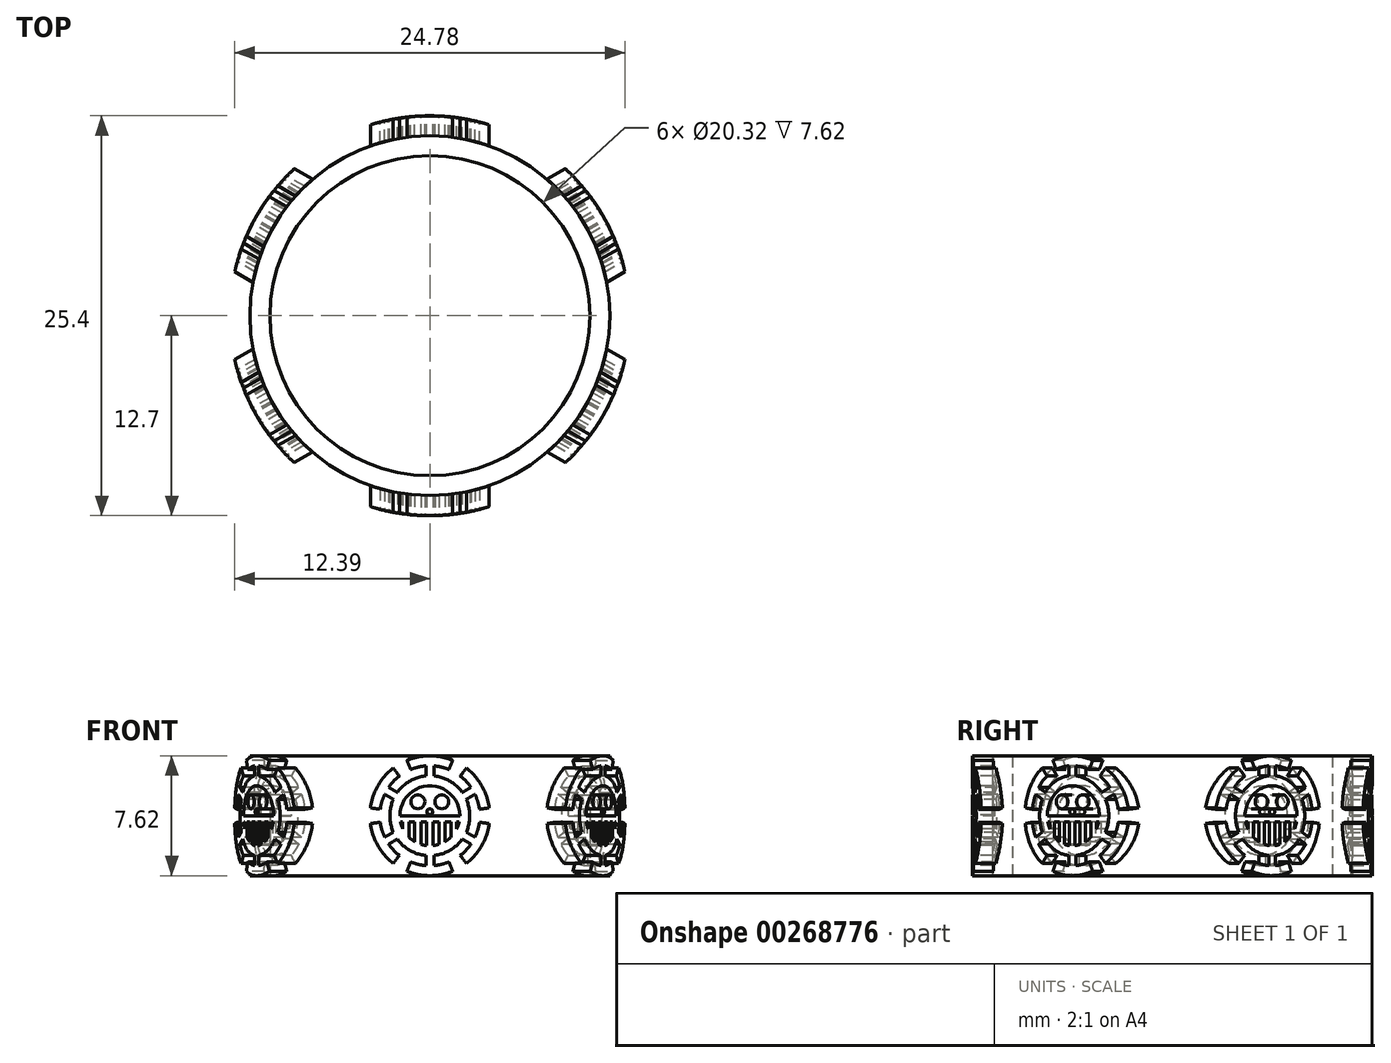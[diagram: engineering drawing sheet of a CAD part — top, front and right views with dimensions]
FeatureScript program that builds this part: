
annotation { "Feature Type Name" : "Feature", "Feature Type Description" : "" }
export const myFeature = defineFeature(function(context is Context, id is Id, definition is map)
    precondition{}
    {
        {
            var Q0;
            Q0=qCreatedBy(makeId("Front.planeOp"),FACE);
            var sketch = newSketch(context, id + "F0", { "sketchPlane" : qUnion([Q0])});
            skCircle(sketch, "E0", {"center": v(0, 3.81) * mm, "radius": 3.81 * mm});
            skSolve(sketch);
        }
        {
            var Q0;
            Q0 = qSketchRegion(id + "F0", true);
            extrude(context, id + "F1", {"entities" : qUnion([Q0]), "depth" : 13.97 * mm});
        }
        {
            var Q0;
            Q0=makeQuery(id+"F1.opExtrude","CAP_FACE",FACE,{"disambiguationData":[OSD([sQuery(id+"F0.wireOp",EDGE,"E0")])],"isStart":false});
            var sketch = newSketch(context, id + "F2", { "sketchPlane" : qUnion([Q0])});
            skArc(sketch, "E1", {"start": v(-1.93, 6.33) * mm, "mid": v(-2.3, 6) * mm, "end": v(-2.61, 5.61) * mm});
            skLineSegment(sketch, "E2", {"start": v(-1.22, 6.74) * mm, "end": v(-1.46, 7.33) * mm});
            skLineSegment(sketch, "E3", {"start": v(1.22, 6.74) * mm, "end": v(1.46, 7.33) * mm});
            skLineSegment(sketch, "E4.1.0", {"start": v(-3.15, 4.22) * mm, "end": v(-3.78, 4.3) * mm});
            skLineSegment(sketch, "E4.1.1", {"start": v(-1.93, 6.33) * mm, "end": v(-2.32, 6.83) * mm});
            skLineSegment(sketch, "E4.2.0", {"start": v(-1.93, 1.3) * mm, "end": v(-2.32, 0.79) * mm});
            skLineSegment(sketch, "E4.2.1", {"start": v(-3.15, 3.4) * mm, "end": v(-3.78, 3.31) * mm});
            skLineSegment(sketch, "E4.3.0", {"start": v(1.22, 0.88) * mm, "end": v(1.46, 0.3) * mm});
            skLineSegment(sketch, "E4.3.1", {"start": v(-1.22, 0.88) * mm, "end": v(-1.46, 0.3) * mm});
            skLineSegment(sketch, "E4.4.0", {"start": v(3.15, 3.4) * mm, "end": v(3.78, 3.31) * mm});
            skLineSegment(sketch, "E4.4.1", {"start": v(1.93, 1.3) * mm, "end": v(2.32, 0.79) * mm});
            skLineSegment(sketch, "E4.5.0", {"start": v(1.93, 6.33) * mm, "end": v(2.32, 6.83) * mm});
            skLineSegment(sketch, "E4.5.1", {"start": v(3.15, 4.22) * mm, "end": v(3.78, 4.3) * mm});
            skPoint(sketch, "E5.orphan", {"position": v(0, 3.8) * mm});
            skArc(sketch, "E6.trimOffspring", {"start": v(1.22, 6.74) * mm, "mid": v(0.74, 6.9) * mm, "end": v(0.25, 6.97) * mm});
            skArc(sketch, "E7.trimOffspring", {"start": v(3.15, 4.22) * mm, "mid": v(3.04, 4.7) * mm, "end": v(2.87, 5.17) * mm});
            skArc(sketch, "E8.trimOffspring", {"start": v(1.93, 1.3) * mm, "mid": v(2.3, 1.62) * mm, "end": v(2.61, 2) * mm});
            skArc(sketch, "E9.trimOffspring", {"start": v(-1.22, 0.88) * mm, "mid": v(-0.74, 0.72) * mm, "end": v(-0.25, 0.65) * mm});
            skArc(sketch, "E10.trimOffspring", {"start": v(-3.15, 3.4) * mm, "mid": v(-3.04, 2.91) * mm, "end": v(-2.87, 2.45) * mm});
            skArc(sketch, "E11", {"start": v(-0.25, 6.34) * mm, "mid": v(-1.27, 6) * mm, "end": v(-2.06, 5.3) * mm});
            skArc(sketch, "E12", {"start": v(-1.87, 3.43) * mm, "mid": v(-1.8, 3.2) * mm, "end": v(-1.71, 2.98) * mm});
            skLineSegment(sketch, "E13", {"start": v(0.25, 6.97) * mm, "end": v(0.25, 6.34) * mm});
            skLineSegment(sketch, "E14.MirrorCS", {"start": v(-0.25, 6.97) * mm, "end": v(-0.25, 6.34) * mm});
            skArc(sketch, "E15.trimOffspring", {"start": v(-0.25, 6.97) * mm, "mid": v(-0.74, 6.9) * mm, "end": v(-1.22, 6.74) * mm});
            skPoint(sketch, "E16.orphan", {"position": v(-0.25, 5.7) * mm});
            skPoint(sketch, "E17.orphan", {"position": v(0.25, 5.7) * mm});
            skLineSegment(sketch, "E18.1.0", {"start": v(-2.61, 5.61) * mm, "end": v(-2.06, 5.3) * mm});
            skLineSegment(sketch, "E18.1.1", {"start": v(-2.87, 5.17) * mm, "end": v(-2.32, 4.85) * mm});
            skLineSegment(sketch, "E18.2.0", {"start": v(-2.87, 2.45) * mm, "end": v(-2.32, 2.77) * mm});
            skLineSegment(sketch, "E18.2.1", {"start": v(-2.61, 2) * mm, "end": v(-2.06, 2.33) * mm});
            skLineSegment(sketch, "E18.3.0", {"start": v(-0.25, 0.65) * mm, "end": v(-0.25, 1.28) * mm});
            skLineSegment(sketch, "E18.3.1", {"start": v(0.25, 0.65) * mm, "end": v(0.25, 1.28) * mm});
            skLineSegment(sketch, "E18.4.0", {"start": v(2.61, 2) * mm, "end": v(2.06, 2.33) * mm});
            skLineSegment(sketch, "E18.4.1", {"start": v(2.87, 2.45) * mm, "end": v(2.32, 2.77) * mm});
            skLineSegment(sketch, "E18.5.0", {"start": v(2.87, 5.17) * mm, "end": v(2.32, 4.85) * mm});
            skLineSegment(sketch, "E18.5.1", {"start": v(2.61, 5.61) * mm, "end": v(2.06, 5.3) * mm});
            skCircle(sketch, "E19", {"center": v(0, 3.81) * mm, "radius": 3.8 * mm});
            skArc(sketch, "E20.trimOffspring", {"start": v(-2.32, 4.85) * mm, "mid": v(-2.54, 3.8) * mm, "end": v(-2.32, 2.77) * mm});
            skArc(sketch, "E21.trimOffspring", {"start": v(-2.87, 5.17) * mm, "mid": v(-3.04, 4.7) * mm, "end": v(-3.15, 4.22) * mm});
            skArc(sketch, "E22.trimOffspring", {"start": v(2.06, 5.3) * mm, "mid": v(1.27, 6) * mm, "end": v(0.25, 6.34) * mm});
            skArc(sketch, "E23.trimOffspring", {"start": v(2.61, 5.61) * mm, "mid": v(2.3, 6) * mm, "end": v(1.93, 6.33) * mm});
            skArc(sketch, "E24.trimOffspring", {"start": v(2.32, 2.77) * mm, "mid": v(2.54, 3.8) * mm, "end": v(2.32, 4.85) * mm});
            skArc(sketch, "E25.trimOffspring", {"start": v(2.87, 2.45) * mm, "mid": v(3.04, 2.91) * mm, "end": v(3.15, 3.4) * mm});
            skArc(sketch, "E26.trimOffspring", {"start": v(0.25, 0.65) * mm, "mid": v(0.74, 0.72) * mm, "end": v(1.22, 0.88) * mm});
            skArc(sketch, "E27.trimOffspring", {"start": v(0.25, 1.28) * mm, "mid": v(1.27, 1.61) * mm, "end": v(2.06, 2.33) * mm});
            skArc(sketch, "E28.trimOffspring", {"start": v(-2.61, 2) * mm, "mid": v(-2.3, 1.62) * mm, "end": v(-1.93, 1.3) * mm});
            skArc(sketch, "E29.trimOffspring", {"start": v(-2.06, 2.33) * mm, "mid": v(-1.27, 1.61) * mm, "end": v(-0.25, 1.28) * mm});
            skLineSegment(sketch, "E30", {"start": v(-1.9, 3.81) * mm, "end": v(1.9, 3.81) * mm});
            skLineSegment(sketch, "E31", {"start": v(-0.2, 3.43) * mm, "end": v(-0.2, 1.91) * mm});
            skLineSegment(sketch, "E32", {"start": v(0.2, 3.43) * mm, "end": v(0.2, 1.91) * mm});
            skLineSegment(sketch, "E33", {"start": v(-0.57, 3.43) * mm, "end": v(-0.57, 2) * mm});
            skLineSegment(sketch, "E34", {"start": v(-0.95, 3.43) * mm, "end": v(-0.95, 2.16) * mm});
            skLineSegment(sketch, "E35", {"start": v(-1.33, 3.43) * mm, "end": v(-1.33, 2.45) * mm});
            skLineSegment(sketch, "E36", {"start": v(-1.71, 3.43) * mm, "end": v(-1.71, 2.98) * mm});
            skLineSegment(sketch, "E37", {"start": v(0.57, 3.43) * mm, "end": v(0.57, 2) * mm});
            skLineSegment(sketch, "E38", {"start": v(0.95, 3.43) * mm, "end": v(0.95, 2.16) * mm});
            skLineSegment(sketch, "E39", {"start": v(1.33, 3.43) * mm, "end": v(1.33, 2.45) * mm});
            skLineSegment(sketch, "E40", {"start": v(1.71, 3.43) * mm, "end": v(1.71, 2.98) * mm});
            skLineSegment(sketch, "E41", {"start": v(-1.87, 3.43) * mm, "end": v(-1.71, 3.43) * mm});
            skArc(sketch, "E42.trimOffspring", {"start": v(1.9, 3.81) * mm, "mid": v(0, 5.71) * mm, "end": v(-1.9, 3.81) * mm});
            skArc(sketch, "E43.trimOffspring", {"start": v(1.71, 2.98) * mm, "mid": v(1.8, 3.2) * mm, "end": v(1.87, 3.43) * mm});
            skLineSegment(sketch, "E44.trimOffspring", {"start": v(1.71, 3.43) * mm, "end": v(1.87, 3.43) * mm});
            skLineSegment(sketch, "E45.trimOffspring", {"start": v(0.95, 3.43) * mm, "end": v(1.33, 3.43) * mm});
            skArc(sketch, "E46.trimOffspring", {"start": v(0.95, 2.16) * mm, "mid": v(1.15, 2.3) * mm, "end": v(1.33, 2.45) * mm});
            skArc(sketch, "E47.trimOffspring", {"start": v(0.2, 1.91) * mm, "mid": v(0.38, 1.94) * mm, "end": v(0.57, 2) * mm});
            skLineSegment(sketch, "E48.trimOffspring", {"start": v(0.2, 3.43) * mm, "end": v(0.57, 3.43) * mm});
            skLineSegment(sketch, "E49.trimOffspring", {"start": v(-0.57, 3.43) * mm, "end": v(-0.2, 3.43) * mm});
            skArc(sketch, "E50.trimOffspring", {"start": v(-0.57, 2) * mm, "mid": v(-0.38, 1.94) * mm, "end": v(-0.2, 1.91) * mm});
            skArc(sketch, "E51.trimOffspring", {"start": v(-1.33, 2.45) * mm, "mid": v(-1.15, 2.3) * mm, "end": v(-0.95, 2.16) * mm});
            skLineSegment(sketch, "E52.trimOffspring", {"start": v(-1.33, 3.43) * mm, "end": v(-0.95, 3.43) * mm});
            skCircle(sketch, "E53", {"center": v(-0.76, 4.7) * mm, "radius": 0.44 * mm});
            skCircle(sketch, "E54", {"center": v(0.76, 4.7) * mm, "radius": 0.44 * mm});
            skCircle(sketch, "E55", {"center": v(0, 4.06) * mm, "radius": 0.2 * mm});
            skSolve(sketch);
        }
        {
            var Q0;
            Q0=makeQuery(id+"F2.imprint","IMPRINT",FACE,{"disambiguationData":[TD([[makeQuery(id+"F2.imprint","IMPRINT",EDGE,{"derivedFrom":sQuery(id+"F2.wireOp",EDGE,"E1")}),1.0]])]});
            var Q1;
            {var subQ1=sQuery(id+"F2.wireOp",EDGE,"E3");Q1=makeQuery(id+"F2.imprint","IMPRINT",FACE,{"disambiguationData":[TD([[makeQuery(id+"F2.imprint","IMPRINT",EDGE,{"derivedFrom":subQ1}),-1.0]])]});}
            var Q2;
            {var subQ2=sQuery(id+"F2.wireOp",EDGE,"E4.1.0");Q2=makeQuery(id+"F2.imprint","IMPRINT",FACE,{"disambiguationData":[TD([[makeQuery(id+"F2.imprint","IMPRINT",EDGE,{"derivedFrom":subQ2}),1.0]])]});}
            var Q3;
            {var subQ1=sQuery(id+"F2.wireOp",EDGE,"E4.2.0");Q3=makeQuery(id+"F2.imprint","IMPRINT",FACE,{"disambiguationData":[TD([[makeQuery(id+"F2.imprint","IMPRINT",EDGE,{"derivedFrom":subQ1}),1.0]])]});}
            var Q4;
            {var subQ1=sQuery(id+"F2.wireOp",EDGE,"E4.3.0");Q4=makeQuery(id+"F2.imprint","IMPRINT",FACE,{"disambiguationData":[TD([[makeQuery(id+"F2.imprint","IMPRINT",EDGE,{"derivedFrom":subQ1}),1.0]])]});}
            var Q5;
            {var subQ0=sQuery(id+"F2.wireOp",EDGE,"E4.4.0");Q5=makeQuery(id+"F2.imprint","IMPRINT",FACE,{"disambiguationData":[TD([[makeQuery(id+"F2.imprint","IMPRINT",EDGE,{"derivedFrom":subQ0}),1.0]])]});}
            var Q6;
            Q6=makeQuery(id+"F2.imprint","IMPRINT",FACE,{"disambiguationData":[TD([[makeQuery(id+"F2.imprint","IMPRINT",EDGE,{"derivedFrom":sQuery(id+"F2.wireOp",EDGE,"E12")}),1.0]])]});
            var Q7;
            Q7=makeQuery(id+"F2.imprint","IMPRINT",FACE,{"disambiguationData":[TD([[makeQuery(id+"F2.imprint","IMPRINT",EDGE,{"derivedFrom":sQuery(id+"F2.wireOp",EDGE,"E34")}),-1.0]])]});
            var Q8;
            Q8=makeQuery(id+"F2.imprint","IMPRINT",FACE,{"disambiguationData":[TD([[makeQuery(id+"F2.imprint","IMPRINT",EDGE,{"derivedFrom":sQuery(id+"F2.wireOp",EDGE,"E31")}),-1.0]])]});
            var Q9;
            Q9=makeQuery(id+"F2.imprint","IMPRINT",FACE,{"disambiguationData":[TD([[makeQuery(id+"F2.imprint","IMPRINT",EDGE,{"derivedFrom":sQuery(id+"F2.wireOp",EDGE,"E32")}),1.0]])]});
            var Q10;
            Q10=makeQuery(id+"F2.imprint","IMPRINT",FACE,{"disambiguationData":[TD([[makeQuery(id+"F2.imprint","IMPRINT",EDGE,{"derivedFrom":sQuery(id+"F2.wireOp",EDGE,"E38")}),1.0]])]});
            var Q11;
            Q11=makeQuery(id+"F2.imprint","IMPRINT",FACE,{"disambiguationData":[TD([[makeQuery(id+"F2.imprint","IMPRINT",EDGE,{"derivedFrom":sQuery(id+"F2.wireOp",EDGE,"E30")}),1.0]])]});
            var Q12;
            Q12=makeQuery(id+"F2.imprint","IMPRINT",FACE,{"disambiguationData":[TD([[makeQuery(id+"F2.imprint","IMPRINT",EDGE,{"derivedFrom":sQuery(id+"F2.wireOp",EDGE,"E40")}),1.0]])]});
            extrude(context, id + "F3", {"entities" : qUnion([Q0, Q1, Q2, Q3, Q4, Q5, Q6, Q7, Q8, Q9, Q10, Q11, Q12]), "operationType" : NewBodyOperationType.REMOVE, "oppositeDirection" : true, "depth" : 50.8 * mm});
        }
        {
            var Q0;
            Q0=qCreatedBy(makeId("Top.planeOp"),FACE);
            var sketch = newSketch(context, id + "F4", { "sketchPlane" : qUnion([Q0])});
            skCircle(sketch, "E56", {"center": v(0, 0) * mm, "radius": 10.16 * mm});
            skCircle(sketch, "E57", {"center": v(0, 0) * mm, "radius": 11.43 * mm});
            skSolve(sketch);
        }
        {
            var Q0;
            Q0 = qSketchRegion(id + "F4", true);
            extrude(context, id + "F5", {"entities" : qUnion([Q0]), "operationType" : NewBodyOperationType.ADD, "depth" : 7.62 * mm});
        }
        {
            var Q0;
            Q0=makeQuery(id+"F5.opExtrude","CAP_FACE",FACE,{"disambiguationData":[OSD([sQuery(id+"F4.wireOp",EDGE,"E56"),sQuery(id+"F4.wireOp",EDGE,"E57")])],"isStart":false});
            var sketch = newSketch(context, id + "F6", { "sketchPlane" : qUnion([Q0])});
            skCircle(sketch, "E58", {"center": v(0, 0) * mm, "radius": 16.79 * mm});
            skCircle(sketch, "E59", {"center": v(0, 0) * mm, "radius": 12.7 * mm});
            skSolve(sketch);
        }
        {
            var Q0;
            Q0 = qSketchRegion(id + "F6", true);
            extrude(context, id + "F7", {"entities" : qUnion([Q0]), "operationType" : NewBodyOperationType.REMOVE, "endBound" : BoundingType.THROUGH_ALL, "oppositeDirection" : true, "depth" : 25.4 * mm});
        }
        {
            var Q0;
            Q0=makeQuery(id+"F5.opExtrude","CAP_FACE",FACE,{"disambiguationData":[OSD([sQuery(id+"F4.wireOp",EDGE,"E56"),sQuery(id+"F4.wireOp",EDGE,"E57")])],"isStart":false});
            var sketch = newSketch(context, id + "F8", { "sketchPlane" : qUnion([Q0])});
            skCircle(sketch, "E60", {"center": v(0, 0) * mm, "radius": 10.16 * mm});
            skSolve(sketch);
        }
        {
            var Q0;
            Q0 = qSketchRegion(id + "F8", true);
            extrude(context, id + "F9", {"entities" : qUnion([Q0]), "operationType" : NewBodyOperationType.REMOVE, "endBound" : BoundingType.THROUGH_ALL, "oppositeDirection" : true, "depth" : 25.4 * mm});
        }
        {
            var Q0;
            Q0=qCreatedBy(makeId("Front.planeOp"),FACE);
            var sketch = newSketch(context, id + "F10", { "sketchPlane" : qUnion([Q0])});
            skLineSegment(sketch, "E61", {"start": v(0, 0) * mm, "end": v(0, 33.81) * mm, "construction": true});
            skSolve(sketch);
        }
        {
            var Q0;
            Q0=makeQuery(id+"F3.boolean.opBoolean","SPLIT",BODY,{"disambiguationData":[OD(0.0)],"derivedFrom":makeQuery(id+"F1.opExtrude","SWEPT_BODY",BODY,{"disambiguationData":[OSD([sQuery(id+"F0.wireOp",EDGE,"E0")])]})});
            var Q1;
            Q1=sQuery(id+"F10.wireOp",EDGE,"E61");
            circularPattern(context, id + "F11", {"entities" : qUnion([Q0]), "axis" : qUnion([Q1]), "angle" : 360 * degree, "instanceCount" : 6, "equalSpace" : true});
        }
    });
